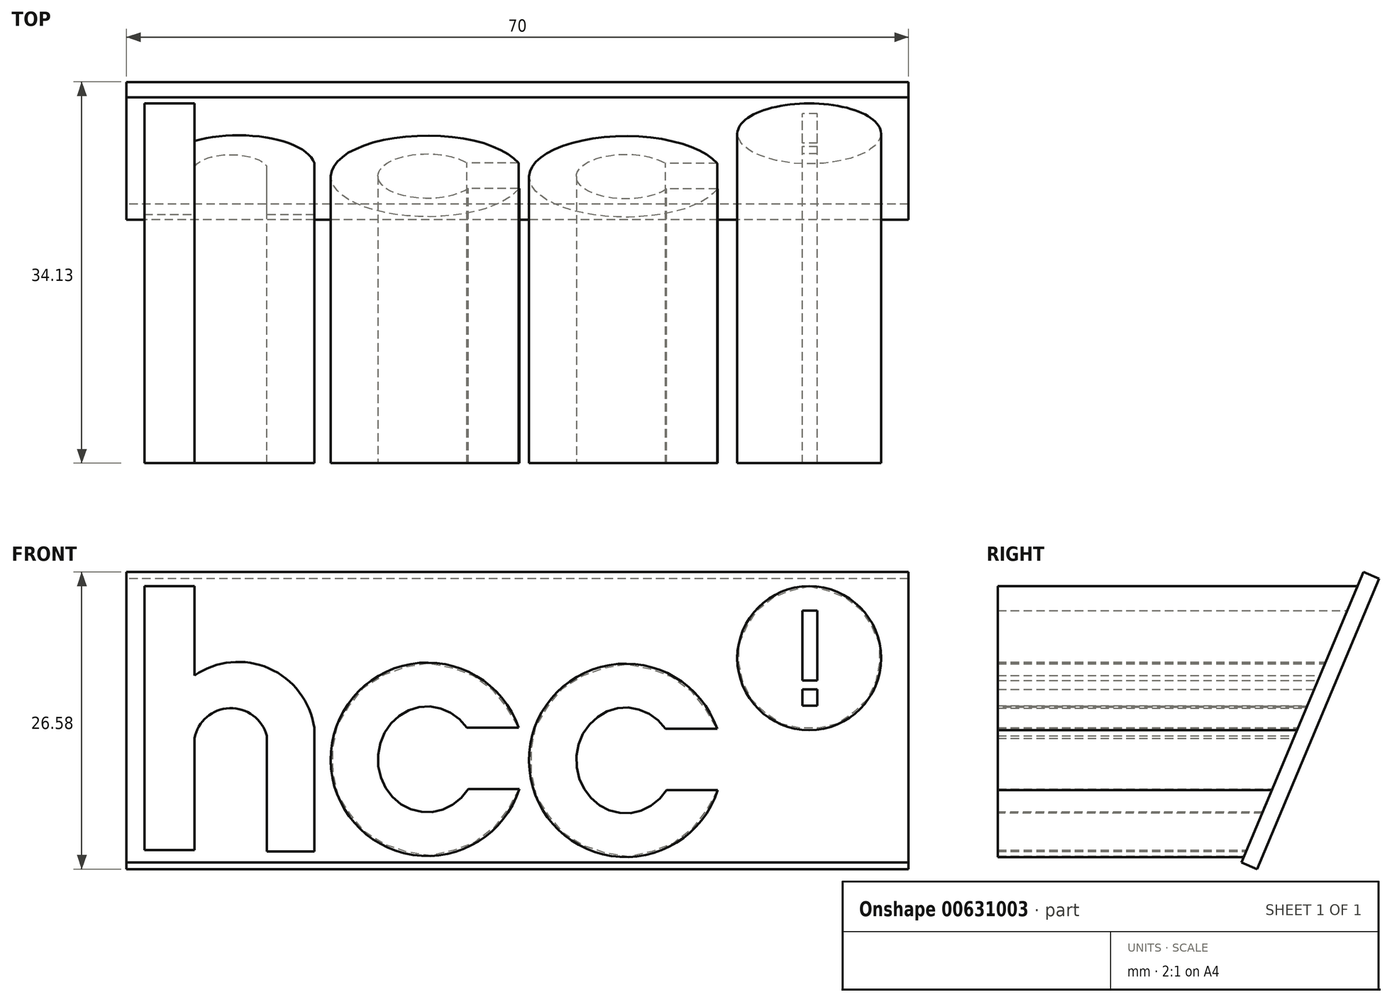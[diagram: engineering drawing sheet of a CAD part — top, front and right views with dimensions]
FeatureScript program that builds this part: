
annotation { "Feature Type Name" : "Feature", "Feature Type Description" : "" }
export const myFeature = defineFeature(function(context is Context, id is Id, definition is map)
    precondition{}
    {
        {
            var Q0;
            Q0=qCreatedBy(makeId("Front.planeOp"),FACE);
            var sketch = newSketch(context, id + "F0", { "sketchPlane" : qUnion([Q0])});
            skLineSegment(sketch, "E0.bottom", {"start": v(-28.92, -14.64) * mm, "end": v(-33.4, -14.64) * mm});
            skLineSegment(sketch, "E0.top", {"start": v(-28.92, -38.27) * mm, "end": v(-33.4, -38.27) * mm});
            skLineSegment(sketch, "E0.left", {"start": v(-28.92, -14.64) * mm, "end": v(-28.92, -22.65) * mm});
            skLineSegment(sketch, "E0.right", {"start": v(-33.4, -14.64) * mm, "end": v(-33.4, -38.27) * mm});
            skArc(sketch, "E1", {"start": v(-18.2, -27.33) * mm, "mid": v(-22.26, -22) * mm, "end": v(-28.92, -22.65) * mm});
            skArc(sketch, "E2", {"start": v(-22.44, -28.05) * mm, "mid": v(-25.77, -25.57) * mm, "end": v(-28.92, -28.27) * mm});
            skLineSegment(sketch, "E3", {"start": v(-22.44, -28.05) * mm, "end": v(-22.44, -38.39) * mm});
            skLineSegment(sketch, "E4", {"start": v(-22.44, -38.39) * mm, "end": v(-18.2, -38.39) * mm});
            skLineSegment(sketch, "E5", {"start": v(-18.2, -38.39) * mm, "end": v(-18.2, -27.33) * mm});
            skArc(sketch, "E6", {"start": v(0.1, -27.33) * mm, "mid": v(-16.73, -30.24) * mm, "end": v(0.16, -32.8) * mm});
            skEllipticalArc(sketch, "E7", {});
            skLineSegment(sketch, "E8", {"start": v(-4.53, -27.33) * mm, "end": v(0.3, -27.33) * mm});
            skLineSegment(sketch, "E9", {"start": v(-4.41, -32.8) * mm, "end": v(0.3, -32.8) * mm});
            skArc(sketch, "E10", {"start": v(17.87, -27.42) * mm, "mid": v(1.03, -30.33) * mm, "end": v(17.93, -32.89) * mm});
            skEllipticalArc(sketch, "E11", {});
            skLineSegment(sketch, "E12", {"start": v(13.24, -27.42) * mm, "end": v(18.07, -27.42) * mm});
            skLineSegment(sketch, "E13", {"start": v(13.35, -32.89) * mm, "end": v(18.07, -32.89) * mm});
            skCircle(sketch, "E14", {"center": v(26.11, -21.1) * mm, "radius": 6.44 * mm});
            skLineSegment(sketch, "E15.bottom", {"start": v(25.52, -16.84) * mm, "end": v(26.84, -16.84) * mm});
            skLineSegment(sketch, "E15.top", {"start": v(25.52, -23.09) * mm, "end": v(26.84, -23.09) * mm});
            skLineSegment(sketch, "E15.left", {"start": v(25.52, -16.84) * mm, "end": v(25.52, -23.09) * mm});
            skLineSegment(sketch, "E15.right", {"start": v(26.84, -16.84) * mm, "end": v(26.84, -23.09) * mm});
            skLineSegment(sketch, "E16.bottom", {"start": v(25.52, -23.88) * mm, "end": v(26.84, -23.88) * mm});
            skLineSegment(sketch, "E16.top", {"start": v(25.52, -25.35) * mm, "end": v(26.84, -25.35) * mm});
            skLineSegment(sketch, "E16.left", {"start": v(25.52, -23.88) * mm, "end": v(25.52, -25.35) * mm});
            skLineSegment(sketch, "E16.right", {"start": v(26.84, -23.88) * mm, "end": v(26.84, -25.35) * mm});
            skPoint(sketch, "E17.orphan", {"position": v(-31.83, -27.33) * mm});
            skLineSegment(sketch, "E18.trimOffspring", {"start": v(-28.92, -28.27) * mm, "end": v(-28.92, -38.27) * mm});
            const initialGuessF0  = {"E7": [-0.008079084567725658, -0.030148023739457127, 0, 1, 0.004734611138701439, 0.0044216665190650265, 5.350779379737523, 4.11952951118792], "E11": [0.009684779681265354, -0.03024211735464632, 0, 1, 0.004734611138701439, 0.0044216665190650265, 5.350779379737523, 4.11952951118792]};
            skSetInitialGuess(sketch, initialGuessF0);
            skSolve(sketch);
        }
        {
            var Q0;
            Q0=makeQuery(id+"F0.imprint","IMPRINT",FACE,{"disambiguationData":[TD([[makeQuery(id+"F0.imprint","IMPRINT",EDGE,{"derivedFrom":sQuery(id+"F0.wireOp",EDGE,"E0.bottom")}),1.0]])]});
            var Q1;
            {var subQ0=sQuery(id+"F0.wireOp",EDGE,"E6");Q1=makeQuery(id+"F0.imprint","IMPRINT",FACE,{"disambiguationData":[TD([[makeQuery(id+"F0.imprint","IMPRINT",EDGE,{"derivedFrom":subQ0}),1.0]])]});}
            var Q2;
            {var subQ0=sQuery(id+"F0.wireOp",EDGE,"E10");Q2=makeQuery(id+"F0.imprint","IMPRINT",FACE,{"disambiguationData":[TD([[makeQuery(id+"F0.imprint","IMPRINT",EDGE,{"derivedFrom":subQ0}),1.0]])]});}
            var Q3;
            Q3=makeQuery(id+"F0.imprint","IMPRINT",FACE,{"disambiguationData":[TD([[makeQuery(id+"F0.imprint","IMPRINT",EDGE,{"derivedFrom":sQuery(id+"F0.wireOp",EDGE,"E14")}),1.0]])]});
            extrude(context, id + "F1", {"entities" : qUnion([Q0, Q1, Q2, Q3]), "depth" : 40 * mm, "offsetDistance" : 25 * mm});
        }
        {
            var Q0;
            Q0=makeQuery(id+"F1.opExtrude","CAP_FACE",FACE,{"disambiguationData":[OSD([sQuery(id+"F0.wireOp",EDGE,"E10"),sQuery(id+"F0.wireOp",EDGE,"E11"),sQuery(id+"F0.wireOp",EDGE,"E12"),sQuery(id+"F0.wireOp",EDGE,"E13")])],"isStart":true});
            var Q1;
            Q1=makeQuery(id+"F1.opExtrude","CAP_EDGE",EDGE,{"disambiguationData":[OSD([sQuery(id+"F0.wireOp",EDGE,"E6")])],"isStart":true});
            var Q2;
            Q2=makeQuery(id+"F1.opExtrude","CAP_EDGE",EDGE,{"disambiguationData":[OSD([sQuery(id+"F0.wireOp",EDGE,"E14")])],"isStart":true});
            var Q3;
            Q3=makeQuery(id+"F1.opExtrude","CAP_EDGE",EDGE,{"disambiguationData":[OSD([sQuery(id+"F0.wireOp",EDGE,"E15.left")])],"isStart":true});
            var Q4;
            Q4=makeQuery(id+"F1.opExtrude","CAP_EDGE",EDGE,{"disambiguationData":[OSD([sQuery(id+"F0.wireOp",EDGE,"E15.bottom")])],"isStart":true});
            var Q5;
            Q5=makeQuery(id+"F1.opExtrude","CAP_EDGE",EDGE,{"disambiguationData":[OSD([sQuery(id+"F0.wireOp",EDGE,"E15.right")])],"isStart":true});
            var Q6;
            Q6=makeQuery(id+"F1.opExtrude","CAP_EDGE",EDGE,{"disambiguationData":[OSD([sQuery(id+"F0.wireOp",EDGE,"E15.top")])],"isStart":true});
            var Q7;
            Q7=makeQuery(id+"F1.opExtrude","CAP_EDGE",EDGE,{"disambiguationData":[OSD([sQuery(id+"F0.wireOp",EDGE,"E16.bottom")])],"isStart":true});
            var Q8;
            Q8=makeQuery(id+"F1.opExtrude","CAP_EDGE",EDGE,{"disambiguationData":[OSD([sQuery(id+"F0.wireOp",EDGE,"E16.left")])],"isStart":true});
            var Q9;
            Q9=makeQuery(id+"F1.opExtrude","CAP_EDGE",EDGE,{"disambiguationData":[OSD([sQuery(id+"F0.wireOp",EDGE,"E16.top")])],"isStart":true});
            var Q10;
            Q10=makeQuery(id+"F1.opExtrude","CAP_EDGE",EDGE,{"disambiguationData":[OSD([sQuery(id+"F0.wireOp",EDGE,"E16.right")])],"isStart":true});
            var Q11;
            Q11=makeQuery(id+"F1.opExtrude","CAP_EDGE",EDGE,{"disambiguationData":[OSD([sQuery(id+"F0.wireOp",EDGE,"E5")])],"isStart":true});
            var Q12;
            Q12=makeQuery(id+"F1.opExtrude","CAP_EDGE",EDGE,{"disambiguationData":[OSD([sQuery(id+"F0.wireOp",EDGE,"E1")])],"isStart":true});
            var Q13;
            Q13=makeQuery(id+"F1.opExtrude","CAP_EDGE",EDGE,{"disambiguationData":[OSD([sQuery(id+"F0.wireOp",EDGE,"E0.left")])],"isStart":true});
            var Q14;
            Q14=makeQuery(id+"F1.opExtrude","CAP_EDGE",EDGE,{"disambiguationData":[OSD([sQuery(id+"F0.wireOp",EDGE,"E0.bottom")])],"isStart":true});
            var Q15;
            Q15=makeQuery(id+"F1.opExtrude","CAP_EDGE",EDGE,{"disambiguationData":[OSD([sQuery(id+"F0.wireOp",EDGE,"E0.right")])],"isStart":true});
            var Q16;
            Q16=makeQuery(id+"F1.opExtrude","CAP_EDGE",EDGE,{"disambiguationData":[OSD([sQuery(id+"F0.wireOp",EDGE,"E0.top")])],"isStart":true});
            var Q17;
            Q17=makeQuery(id+"F1.opExtrude","CAP_EDGE",EDGE,{"disambiguationData":[OSD([sQuery(id+"F0.wireOp",EDGE,"E18.trimOffspring")])],"isStart":true});
            var Q18;
            Q18=makeQuery(id+"F1.opExtrude","CAP_EDGE",EDGE,{"disambiguationData":[OSD([sQuery(id+"F0.wireOp",EDGE,"E2")])],"isStart":true});
            var Q19;
            Q19=makeQuery(id+"F1.opExtrude","CAP_EDGE",EDGE,{"disambiguationData":[OSD([sQuery(id+"F0.wireOp",EDGE,"E3")])],"isStart":true});
            var Q20;
            Q20=makeQuery(id+"F1.opExtrude","CAP_EDGE",EDGE,{"disambiguationData":[OSD([sQuery(id+"F0.wireOp",EDGE,"E4")])],"isStart":true});
            var Q21;
            Q21=makeQuery(id+"F1.opExtrude","CAP_EDGE",EDGE,{"disambiguationData":[OSD([sQuery(id+"F0.wireOp",EDGE,"E7")])],"isStart":true});
            var Q22;
            Q22=makeQuery(id+"F1.opExtrude","CAP_EDGE",EDGE,{"disambiguationData":[OSD([sQuery(id+"F0.wireOp",EDGE,"E9")])],"isStart":true});
            var Q23;
            Q23=makeQuery(id+"F1.opExtrude","CAP_EDGE",EDGE,{"disambiguationData":[OSD([sQuery(id+"F0.wireOp",EDGE,"E8")])],"isStart":true});
            chamfer(context, id + "F2", {"entities" : qUnion([Q0, Q1, Q2, Q3, Q4, Q5, Q6, Q7, Q8, Q9, Q10, Q11, Q12, Q13, Q14, Q15, Q16, Q17, Q18, Q19, Q20, Q21, Q22, Q23]), "chamferType" : ChamferType.TWO_OFFSETS, "width1" : 2 * mm, "oppositeDirection" : false, "width2" : 0.6 * mm, "tangentPropagation" : true});
        }
        {
            var Q0;
            Q0=qCreatedBy(makeId("Right.planeOp"),FACE);
            var sketch = newSketch(context, id + "F3", { "sketchPlane" : qUnion([Q0])});
            skLineSegment(sketch, "E19", {"start": v(0, 0) * mm, "end": v(-17.69, -42.06) * mm});
            skLineSegment(sketch, "E20", {"start": v(-17.69, -42.06) * mm, "end": v(0, -42.06) * mm});
            skLineSegment(sketch, "E21", {"start": v(-5.87, -13.97) * mm, "end": v(-7.26, -13.39) * mm});
            skLineSegment(sketch, "E22", {"start": v(-7.26, -13.39) * mm, "end": v(-18.2, -39.39) * mm});
            skLineSegment(sketch, "E23", {"start": v(-18.2, -39.39) * mm, "end": v(-16.8, -39.97) * mm});
            skLineSegment(sketch, "E24", {"start": v(-16.8, -39.97) * mm, "end": v(-5.87, -13.97) * mm});
            skLineSegment(sketch, "E25", {"start": v(0, 0) * mm, "end": v(0, -42.06) * mm});
            skSolve(sketch);
        }
        {
            var Q0;
            Q0=makeQuery(id+"F3.imprint","IMPRINT",FACE,{"disambiguationData":[TD([[makeQuery(id+"F3.imprint","IMPRINT",EDGE,{"derivedFrom":sQuery(id+"F3.wireOp",EDGE,"E21")}),1.0]])]});
            extrude(context, id + "F4", {"entities" : qUnion([Q0]), "operationType" : NewBodyOperationType.ADD, "endBound" : BoundingType.SYMMETRIC, "depth" : 70 * mm, "offsetDistance" : 25 * mm});
        }
        {
            var Q0;
            {var subQ0=sQuery(id+"F3.wireOp",EDGE,"E20");Q0=makeQuery(id+"F3.imprint","IMPRINT",FACE,{"disambiguationData":[TD([[makeQuery(id+"F3.imprint","IMPRINT",EDGE,{"derivedFrom":subQ0}),1.0]])]});}
            extrude(context, id + "F5", {"entities" : qUnion([Q0]), "operationType" : NewBodyOperationType.REMOVE, "endBound" : BoundingType.SYMMETRIC, "oppositeDirection" : true, "depth" : 75 * mm, "offsetDistance" : 25 * mm});
        }
    });
